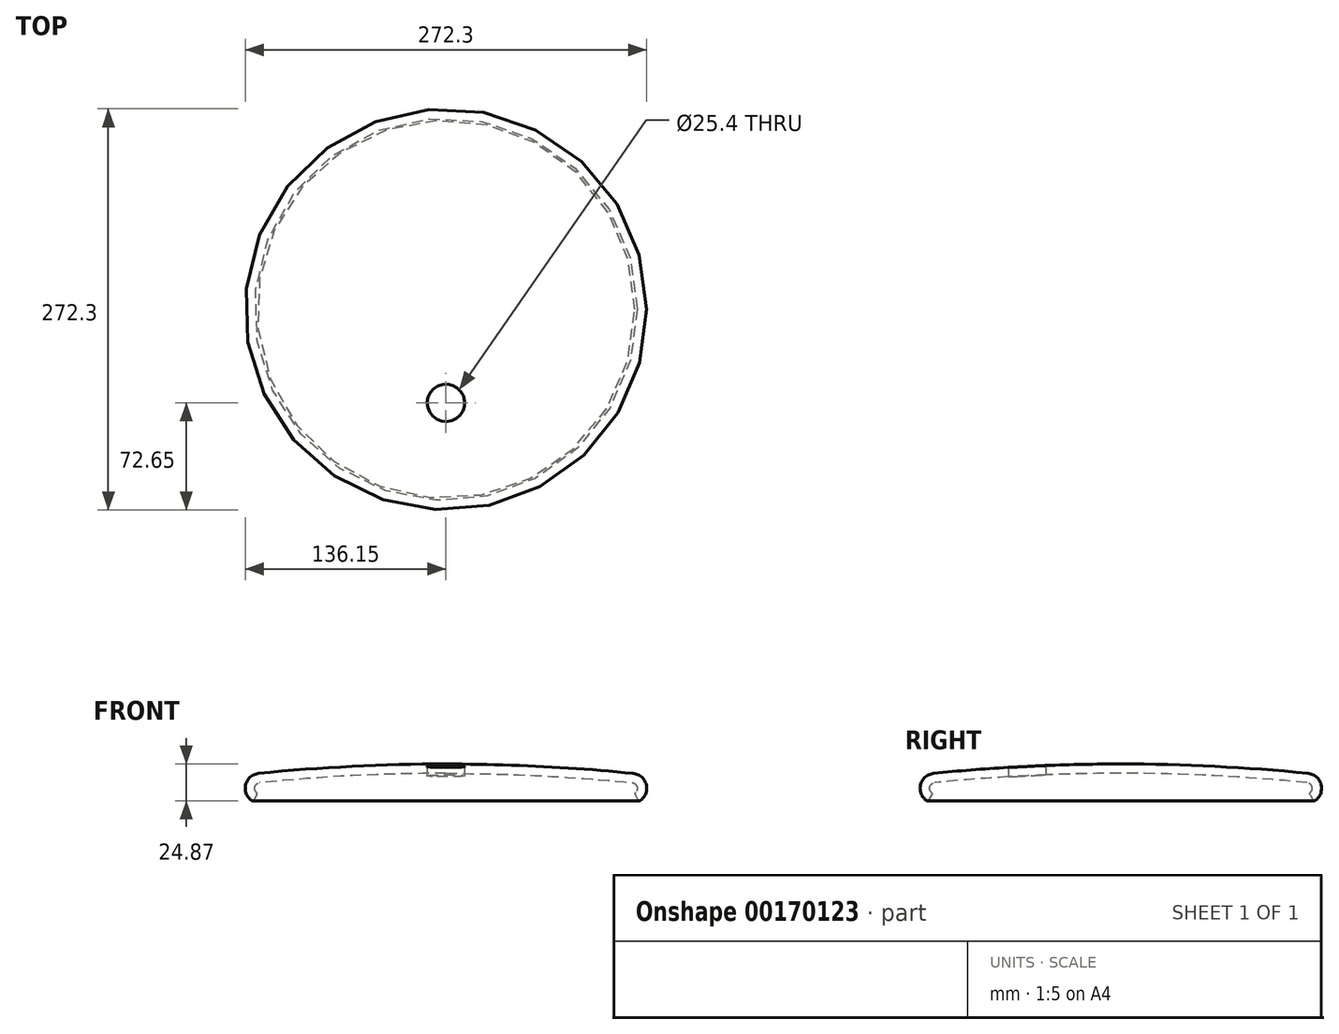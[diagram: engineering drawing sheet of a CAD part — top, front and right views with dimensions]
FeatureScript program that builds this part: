
annotation { "Feature Type Name" : "Feature", "Feature Type Description" : "" }
export const myFeature = defineFeature(function(context is Context, id is Id, definition is map)
    precondition{}
    {
        {
            var Q0;
            Q0=qCreatedBy(makeId("Front.planeOp"),FACE);
            var sketch = newSketch(context, id + "F0", { "sketchPlane" : qUnion([Q0])});
            skLineSegment(sketch, "E0", {"start": v(0, 0) * mm, "end": v(0, 25.4) * mm, "construction": true});
            skLineSegment(sketch, "E1", {"start": v(0, 25.4) * mm, "end": v(-52.86, 25.4) * mm, "construction": true});
            skArc(sketch, "E2", {"start": v(127, 19.05) * mm, "mid": v(63.58, 23.81) * mm, "end": v(0, 25.4) * mm});
            skArc(sketch, "E3", {"start": v(130.81, 0) * mm, "mid": v(135.95, 10.93) * mm, "end": v(127, 19.05) * mm});
            skLineSegment(sketch, "E4", {"start": v(0, 0) * mm, "end": v(240.84, 0) * mm, "construction": true});
            skArc(sketch, "E5.0", {"start": v(126.37, 12.73) * mm, "mid": v(63.26, 17.47) * mm, "end": v(0, 19.05) * mm});
            skArc(sketch, "E5.1", {"start": v(127.8, 5.59) * mm, "mid": v(129.72, 9.69) * mm, "end": v(126.37, 12.73) * mm});
            skLineSegment(sketch, "E6", {"start": v(127.8, 5.59) * mm, "end": v(130.81, 0) * mm});
            skLineSegment(sketch, "E7", {"start": v(0, 25.4) * mm, "end": v(0, 19.05) * mm});
            skSolve(sketch);
        }
        {
            var Q0;
            Q0=makeQuery(id+"F0.imprint","IMPRINT",FACE,{"disambiguationData":[TD([[makeQuery(id+"F0.imprint","IMPRINT",EDGE,{"derivedFrom":sQuery(id+"F0.wireOp",EDGE,"E2")}),1.0]])]});
            var Q1;
            Q1=sQuery(id+"F0.wireOp",EDGE,"E0");
            revolve(context, id + "F1", {"entities" : qUnion([Q0]), "axis" : qUnion([Q1]), "revolveType" : RevolveType.FULL});
        }
        {
            var Q0;
            Q0=makeQuery(id+"F1.opRevolve","SWEPT_EDGE",EDGE,{"disambiguationData":[OSD([sQuery(id+"F0.wireOp",EDGE,"E5.1"),sQuery(id+"F0.wireOp",EDGE,"E6")])]});
            var Q1;
            Q1=makeQuery(id+"F1.opRevolve","SWEPT_EDGE",EDGE,{"disambiguationData":[OSD([sQuery(id+"F0.wireOp",EDGE,"E3"),sQuery(id+"F0.wireOp",EDGE,"E6")])]});
            fillet(context, id + "F2", {"entities" : qUnion([Q0, Q1]), "radius" : 1.27 * mm, "tangentPropagation" : true, "allowEdgeOverflow" : false});
        }
        {
            var Q0;
            Q0=qCreatedBy(makeId("Top.planeOp"),FACE);
            var sketch = newSketch(context, id + "F3", { "sketchPlane" : qUnion([Q0])});
            skLineSegment(sketch, "E8", {"start": v(0, 0) * mm, "end": v(0, -63.5) * mm});
            skCircle(sketch, "E9", {"center": v(0, -63.5) * mm, "radius": 12.7 * mm});
            skSolve(sketch);
        }
        {
            var Q0;
            Q0=makeQuery(id+"F3.imprint","IMPRINT",FACE,{"disambiguationData":[TD([[makeQuery(id+"F3.imprint","IMPRINT",EDGE,{"derivedFrom":sQuery(id+"F3.wireOp",EDGE,"E9")}),1.0]])]});
            extrude(context, id + "F4", {"entities" : qUnion([Q0]), "operationType" : NewBodyOperationType.REMOVE, "depth" : 58.93 * mm});
        }
    });
